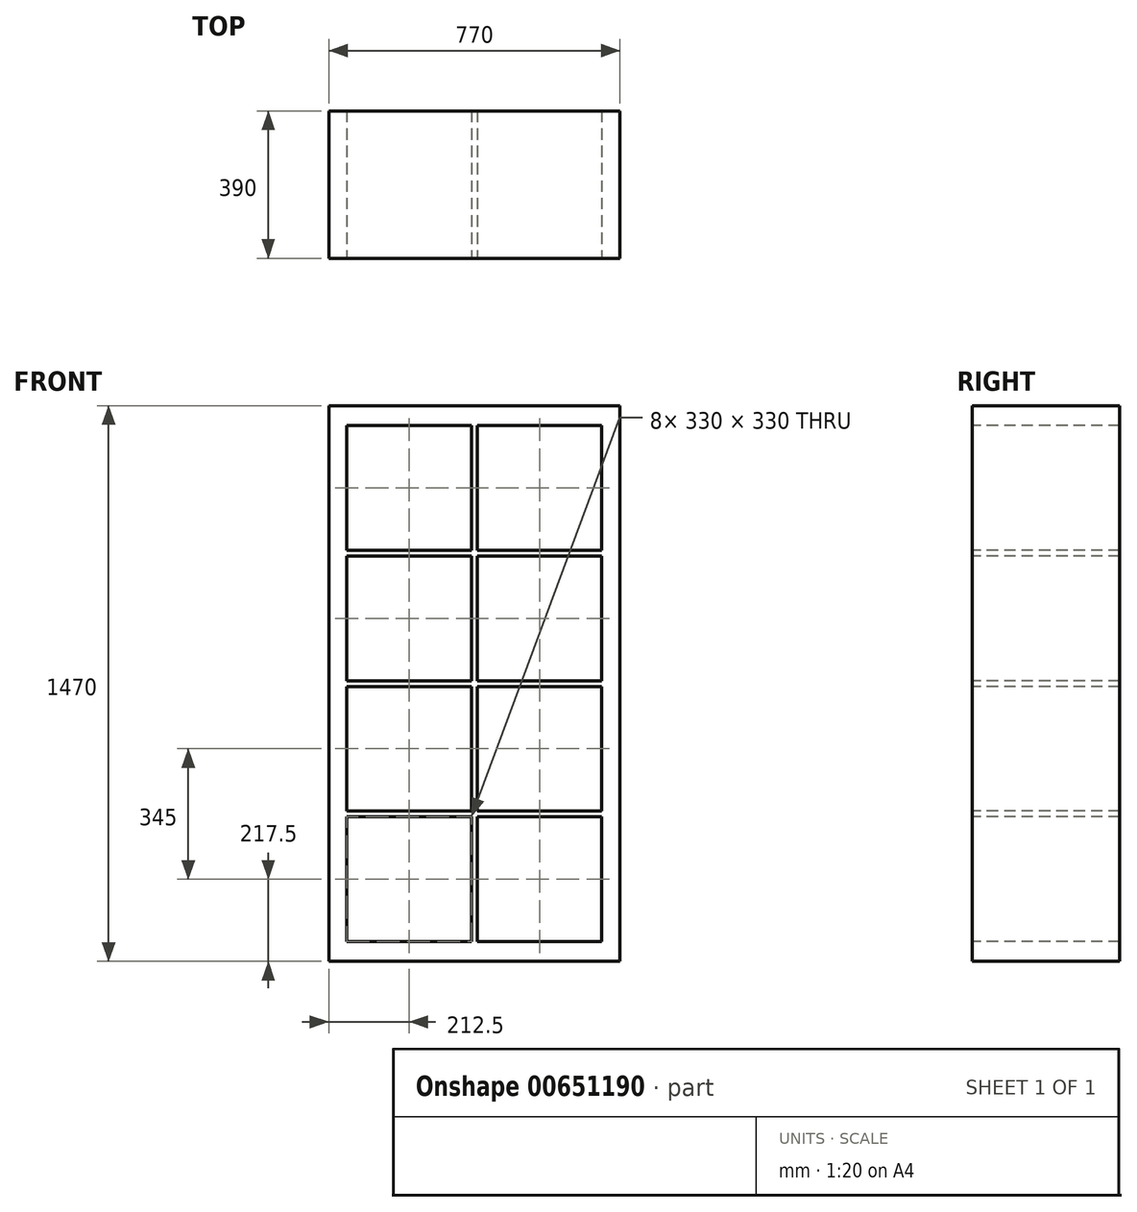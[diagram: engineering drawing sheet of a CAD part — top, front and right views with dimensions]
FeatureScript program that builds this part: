
annotation { "Feature Type Name" : "Feature", "Feature Type Description" : "" }
export const myFeature = defineFeature(function(context is Context, id is Id, definition is map)
    precondition{}
    {
        {
            var Q0;
            Q0=qCreatedBy(makeId("Front.planeOp"),FACE);
            var sketch = newSketch(context, id + "F0", { "sketchPlane" : qUnion([Q0])});
            skLineSegment(sketch, "E0.bottom", {"start": v(0, 0) * mm, "end": v(770, 0) * mm});
            skLineSegment(sketch, "E0.top", {"start": v(0, 1470) * mm, "end": v(770, 1470) * mm});
            skLineSegment(sketch, "E0.left", {"start": v(0, 0) * mm, "end": v(0, 1470) * mm});
            skLineSegment(sketch, "E0.right", {"start": v(770, 0) * mm, "end": v(770, 1470) * mm});
            skSolve(sketch);
        }
        {
            var Q0;
            Q0=qSketchRegion(id+"F0",true);
            extrude(context, id + "F1", {"entities" : qUnion([Q0]), "oppositeDirection" : true, "depth" : 390 * mm});
        }
        {
            var Q0;
            Q0=makeQuery(id+"F1.opExtrude","CAP_FACE",FACE,{"disambiguationData":[OSD([sQuery(id+"F0.wireOp",EDGE,"E0.bottom"),sQuery(id+"F0.wireOp",EDGE,"E0.top"),sQuery(id+"F0.wireOp",EDGE,"E0.left"),sQuery(id+"F0.wireOp",EDGE,"E0.right")])],"isStart":true});
            var sketch = newSketch(context, id + "F2", { "sketchPlane" : qUnion([Q0])});
            skLineSegment(sketch, "E1.bottom", {"start": v(47.5, 397.5) * mm, "end": v(377.5, 397.5) * mm});
            skLineSegment(sketch, "E1.top", {"start": v(47.5, 727.5) * mm, "end": v(377.5, 727.5) * mm});
            skLineSegment(sketch, "E1.left", {"start": v(47.5, 397.5) * mm, "end": v(47.5, 727.5) * mm});
            skLineSegment(sketch, "E1.right", {"start": v(377.5, 397.5) * mm, "end": v(377.5, 727.5) * mm});
            skPoint(sketch, "E2", {"position": v(385, 1470) * mm});
            skPoint(sketch, "E3", {"position": v(385, 0) * mm});
            skLineSegment(sketch, "E4", {"start": v(385, 1470) * mm, "end": v(385, 0) * mm, "construction": true});
            skLineSegment(sketch, "E5", {"start": v(0, 735) * mm, "end": v(770, 735) * mm, "construction": true});
            skLineSegment(sketch, "E6.MirrorCS", {"start": v(392.5, 397.5) * mm, "end": v(392.5, 727.5) * mm});
            skLineSegment(sketch, "E7.MirrorCS", {"start": v(722.5, 727.5) * mm, "end": v(392.5, 727.5) * mm});
            skLineSegment(sketch, "E8.MirrorCS", {"start": v(722.5, 397.5) * mm, "end": v(722.5, 727.5) * mm});
            skLineSegment(sketch, "E9.MirrorCS", {"start": v(722.5, 397.5) * mm, "end": v(392.5, 397.5) * mm});
            skLineSegment(sketch, "E10.MirrorCS", {"start": v(722.5, 742.5) * mm, "end": v(392.5, 742.5) * mm});
            skLineSegment(sketch, "E11.MirrorCS", {"start": v(47.5, 742.5) * mm, "end": v(377.5, 742.5) * mm});
            skLineSegment(sketch, "E12.MirrorCS", {"start": v(47.5, 1072.5) * mm, "end": v(47.5, 742.5) * mm});
            skLineSegment(sketch, "E13.MirrorCS", {"start": v(377.5, 1072.5) * mm, "end": v(377.5, 742.5) * mm});
            skLineSegment(sketch, "E14.MirrorCS", {"start": v(392.5, 1072.5) * mm, "end": v(392.5, 742.5) * mm});
            skLineSegment(sketch, "E15.MirrorCS", {"start": v(722.5, 1072.5) * mm, "end": v(722.5, 742.5) * mm});
            skLineSegment(sketch, "E16.MirrorCS", {"start": v(47.5, 1072.5) * mm, "end": v(377.5, 1072.5) * mm});
            skLineSegment(sketch, "E17.MirrorCS", {"start": v(722.5, 1072.5) * mm, "end": v(392.5, 1072.5) * mm});
            skLineSegment(sketch, "E18", {"start": v(0, 1080) * mm, "end": v(770, 1080) * mm, "construction": true});
            skLineSegment(sketch, "E19.MirrorCS", {"start": v(47.5, 1087.5) * mm, "end": v(377.5, 1087.5) * mm});
            skLineSegment(sketch, "E20.MirrorCS", {"start": v(722.5, 1087.5) * mm, "end": v(392.5, 1087.5) * mm});
            skLineSegment(sketch, "E21.MirrorCS", {"start": v(722.5, 1087.5) * mm, "end": v(722.5, 1417.5) * mm});
            skLineSegment(sketch, "E22.MirrorCS", {"start": v(392.5, 1087.5) * mm, "end": v(392.5, 1417.5) * mm});
            skLineSegment(sketch, "E23.MirrorCS", {"start": v(377.5, 1087.5) * mm, "end": v(377.5, 1417.5) * mm});
            skLineSegment(sketch, "E24.MirrorCS", {"start": v(47.5, 1087.5) * mm, "end": v(47.5, 1417.5) * mm});
            skLineSegment(sketch, "E25.MirrorCS", {"start": v(47.5, 1417.5) * mm, "end": v(377.5, 1417.5) * mm});
            skLineSegment(sketch, "E26.MirrorCS", {"start": v(722.5, 1417.5) * mm, "end": v(392.5, 1417.5) * mm});
            skLineSegment(sketch, "E27.MirrorCS", {"start": v(0, 390) * mm, "end": v(770, 390) * mm, "construction": true});
            skLineSegment(sketch, "E28.MirrorCS", {"start": v(47.5, 382.5) * mm, "end": v(377.5, 382.5) * mm});
            skLineSegment(sketch, "E29.MirrorCS", {"start": v(722.5, 382.5) * mm, "end": v(392.5, 382.5) * mm});
            skLineSegment(sketch, "E30.MirrorCS", {"start": v(722.5, 382.5) * mm, "end": v(722.5, 52.5) * mm});
            skLineSegment(sketch, "E31.MirrorCS", {"start": v(392.5, 382.5) * mm, "end": v(392.5, 52.5) * mm});
            skLineSegment(sketch, "E32.MirrorCS", {"start": v(377.5, 382.5) * mm, "end": v(377.5, 52.5) * mm});
            skLineSegment(sketch, "E33.MirrorCS", {"start": v(47.5, 382.5) * mm, "end": v(47.5, 52.5) * mm});
            skLineSegment(sketch, "E34.MirrorCS", {"start": v(47.5, 52.5) * mm, "end": v(377.5, 52.5) * mm});
            skLineSegment(sketch, "E35.MirrorCS", {"start": v(722.5, 52.5) * mm, "end": v(392.5, 52.5) * mm});
            skSolve(sketch);
        }
        {
            var Q0;
            Q0=qSketchRegion(id+"F2",true);
            extrude(context, id + "F3", {"entities" : qUnion([Q0]), "operationType" : NewBodyOperationType.REMOVE, "endBound" : BoundingType.UP_TO_NEXT, "oppositeDirection" : true, "depth" : 25 * mm});
        }
    });
